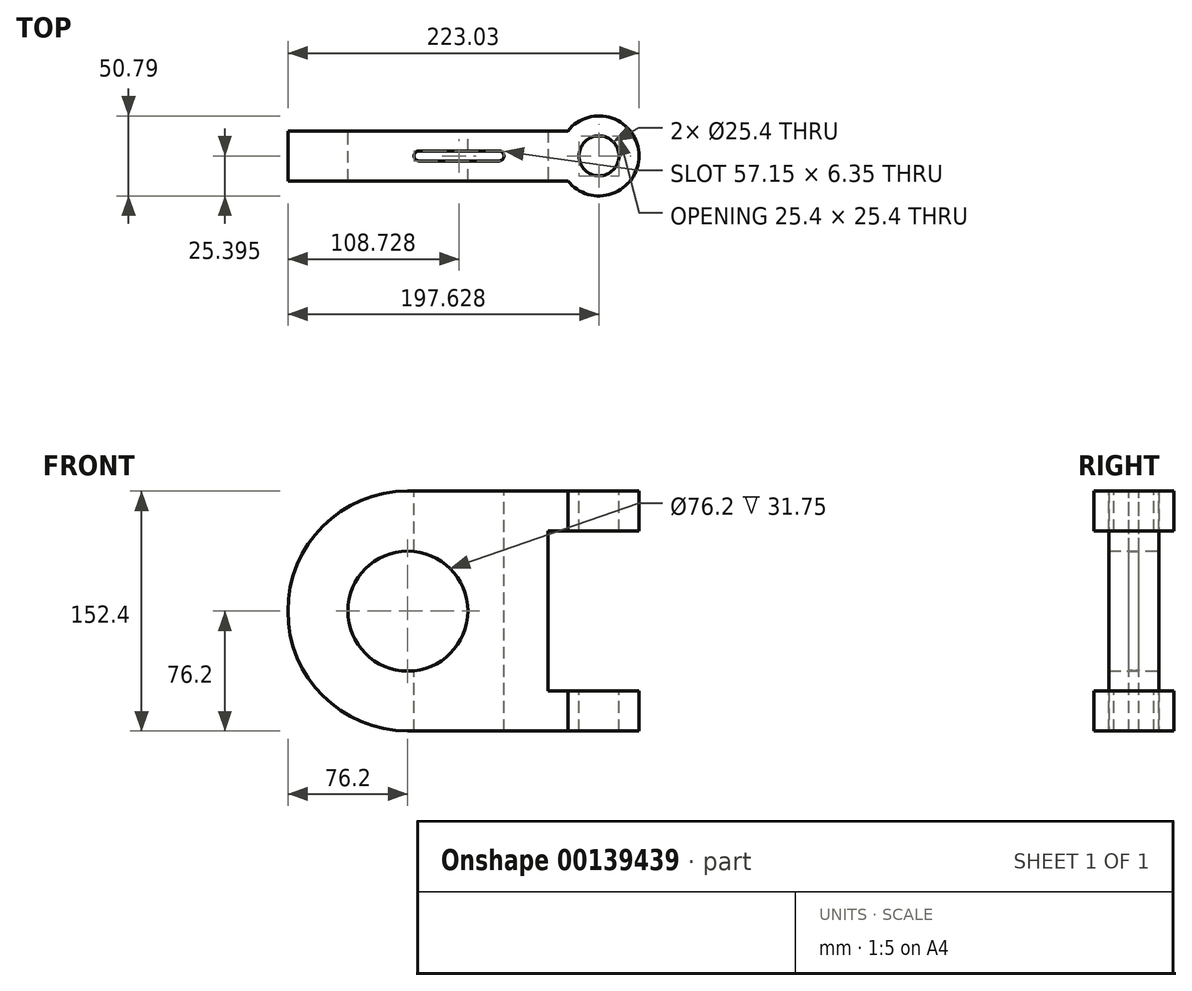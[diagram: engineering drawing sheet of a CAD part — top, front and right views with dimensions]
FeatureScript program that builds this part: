
annotation { "Feature Type Name" : "Feature", "Feature Type Description" : "" }
export const myFeature = defineFeature(function(context is Context, id is Id, definition is map)
    precondition{}
    {
        {
            var Q0;
            Q0=qCreatedBy(makeId("Front.planeOp"),FACE);
            var sketch = newSketch(context, id + "F0", { "sketchPlane" : qUnion([Q0])});
            skCircle(sketch, "E0", {"center": v(0, 0) * mm, "radius": 76.2 * mm});
            skCircle(sketch, "E1", {"center": v(0, 0) * mm, "radius": 38.1 * mm});
            skLineSegment(sketch, "E2", {"start": v(0, 76.2) * mm, "end": v(101.6, 76.2) * mm});
            skLineSegment(sketch, "E3", {"start": v(0, -76.2) * mm, "end": v(101.6, -76.2) * mm});
            skLineSegment(sketch, "E4", {"start": v(101.6, -76.2) * mm, "end": v(101.6, 76.2) * mm});
            skSolve(sketch);
        }
        {
            var Q0;
            Q0 = qSketchRegion(id + "F0", true);
            var Q1;
            Q1=makeQuery(id+"F0.imprint","IMPRINT",FACE,{"disambiguationData":[TD([[makeQuery(id+"F0.imprint","IMPRINT",EDGE,{"derivedFrom":sQuery(id+"F0.wireOp",EDGE,"E1")}),-1.0]])]});
            extrude(context, id + "F1", {"entities" : qUnion([Q0, Q1]), "depth" : 31.75 * mm});
        }
        {
            var Q0;
            Q0=makeQuery(id+"F1.opExtrude","SWEPT_FACE",FACE,{"disambiguationData":[OSD([sQuery(id+"F0.wireOp",EDGE,"E2")])]});
            var sketch = newSketch(context, id + "F2", { "sketchPlane" : qUnion([Q0])});
            skArc(sketch, "E5", {"start": v(101.6, -31.75) * mm, "mid": v(146.83, -15.88) * mm, "end": v(101.6, 0) * mm});
            skCircle(sketch, "E6", {"center": v(121.43, -15.88) * mm, "radius": 12.7 * mm});
            skSolve(sketch);
        }
        {
            var Q0;
            Q0=makeQuery(id+"F2.imprint","IMPRINT",FACE,{"disambiguationData":[TD([[makeQuery(id+"F2.imprint","IMPRINT",EDGE,{"derivedFrom":sQuery(id+"F2.wireOp",EDGE,"E5")}),1.0]])]});
            extrude(context, id + "F3", {"entities" : qUnion([Q0]), "operationType" : NewBodyOperationType.ADD, "oppositeDirection" : true, "depth" : 152.4 * mm});
        }
        {
            var Q0;
            Q0=makeQuery(id+"F1.opExtrude","CAP_FACE",FACE,{"disambiguationData":[OSD([sQuery(id+"F0.wireOp",EDGE,"E0"),sQuery(id+"F0.wireOp",EDGE,"E1"),sQuery(id+"F0.wireOp",EDGE,"E2"),sQuery(id+"F0.wireOp",EDGE,"E3"),sQuery(id+"F0.wireOp",EDGE,"E4")])],"isStart":false});
            var sketch = newSketch(context, id + "F4", { "sketchPlane" : qUnion([Q0])});
            skLineSegment(sketch, "E7.bottom", {"start": v(88.9, 50.8) * mm, "end": v(202.34, 50.8) * mm});
            skLineSegment(sketch, "E7.top", {"start": v(88.9, -50.8) * mm, "end": v(202.34, -50.8) * mm});
            skLineSegment(sketch, "E7.left", {"start": v(88.9, 50.8) * mm, "end": v(88.9, -50.8) * mm});
            skLineSegment(sketch, "E7.right", {"start": v(202.34, 50.8) * mm, "end": v(202.34, -50.8) * mm});
            skLineSegment(sketch, "E8", {"start": v(127, 77.62) * mm, "end": v(127, -75.68) * mm});
            skSolve(sketch);
        }
        {
            var Q0;
            Q0 = qSketchRegion(id + "F4", true);
            extrude(context, id + "F5", {"entities" : qUnion([Q0]), "operationType" : NewBodyOperationType.REMOVE, "endBound" : BoundingType.SYMMETRIC, "oppositeDirection" : true, "depth" : 127 * mm});
        }
        {
            var Q0;
            {var subQ0=sQuery(id+"F0.wireOp",EDGE,"E2");Q0=makeQuery(id+"F3.boolean.opBoolean","MERGE",FACE,{"derivedFrom":[makeQuery(id+"F1.opExtrude","SWEPT_FACE",FACE,{"disambiguationData":[OSD([subQ0])]}),makeQuery(id+"F3.opExtrude","CAP_FACE",FACE,{"disambiguationData":[OSD([subQ0,sQuery(id+"F0.wireOp",EDGE,"E4"),sQuery(id+"F2.wireOp",EDGE,"E5"),sQuery(id+"F2.wireOp",EDGE,"E6")])],"isStart":true})]});}
            var sketch = newSketch(context, id + "F6", { "sketchPlane" : qUnion([Q0])});
            skLineSegment(sketch, "E9", {"start": v(121.43, 9.53) * mm, "end": v(121.43, -41.28) * mm});
            skArc(sketch, "E10", {"start": v(57.93, -19.05) * mm, "mid": v(61.1, -15.88) * mm, "end": v(57.93, -12.7) * mm});
            skArc(sketch, "E11", {"start": v(7.13, -12.7) * mm, "mid": v(3.95, -15.88) * mm, "end": v(7.13, -19.05) * mm});
            skLineSegment(sketch, "E12", {"start": v(7.13, -12.7) * mm, "end": v(57.93, -12.7) * mm});
            skLineSegment(sketch, "E13", {"start": v(7.13, -19.05) * mm, "end": v(57.93, -19.05) * mm});
            skSolve(sketch);
        }
        {
            var Q0;
            Q0 = qSketchRegion(id + "F6", true);
            extrude(context, id + "F7", {"entities" : qUnion([Q0]), "operationType" : NewBodyOperationType.REMOVE, "endBound" : BoundingType.THROUGH_ALL, "oppositeDirection" : true, "depth" : 25.4 * mm});
        }
    });
